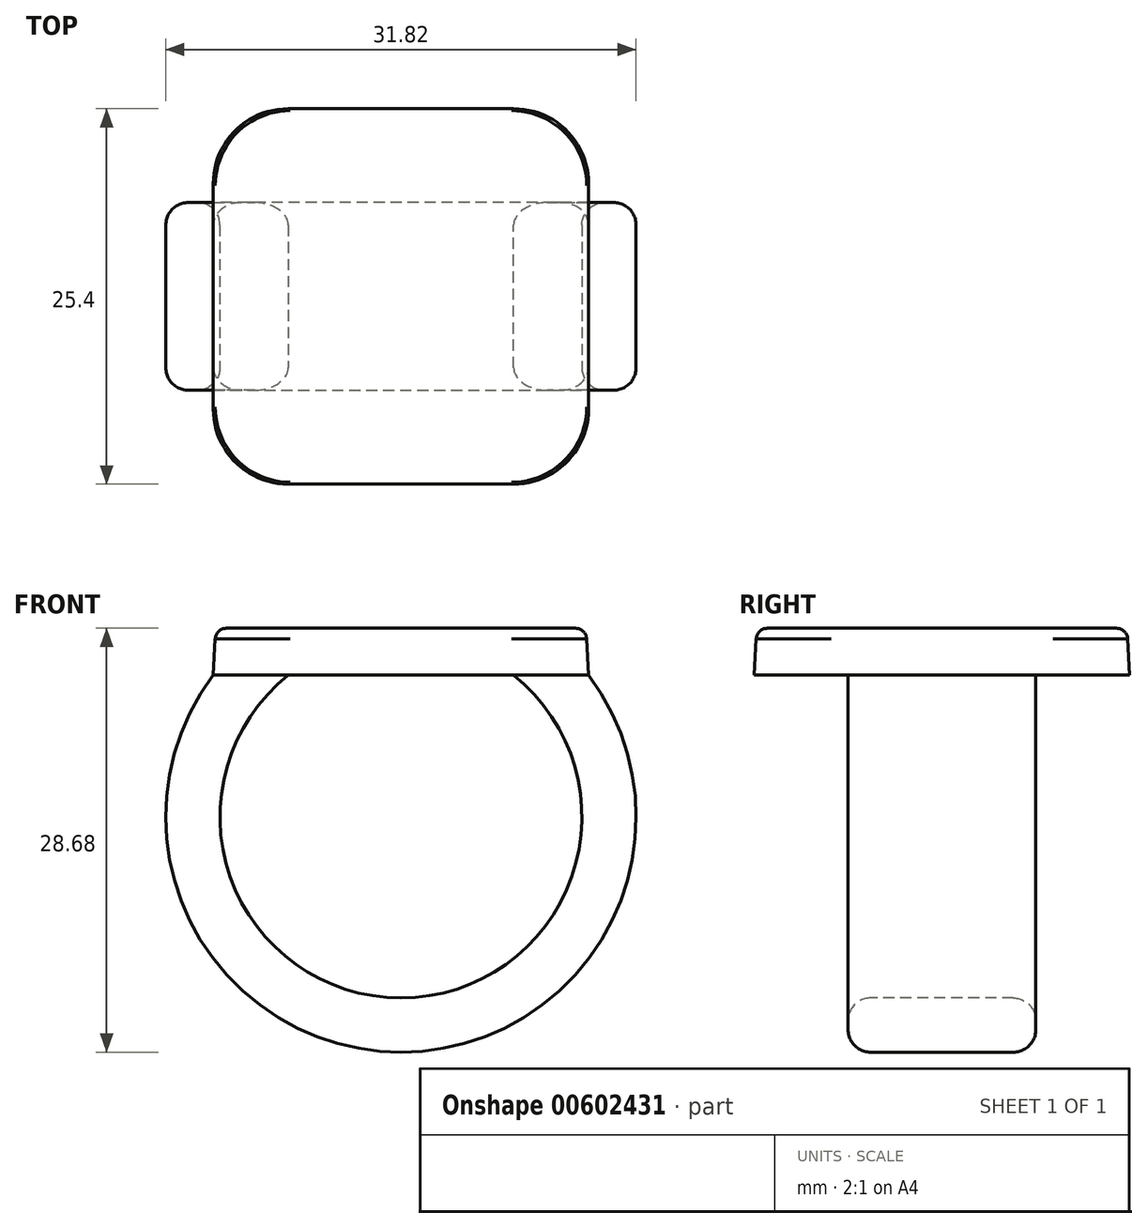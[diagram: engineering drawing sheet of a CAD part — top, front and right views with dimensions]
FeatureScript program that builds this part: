
annotation { "Feature Type Name" : "Feature", "Feature Type Description" : "" }
export const myFeature = defineFeature(function(context is Context, id is Id, definition is map)
    precondition{}
    {
        {
            var Q0;
            Q0=qCreatedBy(makeId("Top.planeOp"),FACE);
            var sketch = newSketch(context, id + "F0", { "sketchPlane" : qUnion([Q0])});
            skLineSegment(sketch, "E0.bottom", {"start": v(12.7, -12.7) * mm, "end": v(-12.7, -12.7) * mm});
            skLineSegment(sketch, "E0.top", {"start": v(12.7, 12.7) * mm, "end": v(-12.7, 12.7) * mm});
            skLineSegment(sketch, "E0.left", {"start": v(12.7, -12.7) * mm, "end": v(12.7, 12.7) * mm});
            skLineSegment(sketch, "E0.right", {"start": v(-12.7, -12.7) * mm, "end": v(-12.7, 12.7) * mm});
            skPoint(sketch, "E0.middle", {"position": v(0, 0) * mm});
            skSolve(sketch);
        }
        {
            var Q0;
            Q0=qSketchRegion(id+"F0",true);
            extrude(context, id + "F1", {"entities" : qUnion([Q0]), "depth" : 3.17 * mm, "offsetDistance" : 25.4 * mm, "hasDraft" : true, "draftAngle" : 3 * degree, "draftPullDirection" : true});
        }
        {
            var Q0;
            Q0=qCreatedBy(makeId("Front.planeOp"),FACE);
            var sketch = newSketch(context, id + "F2", { "sketchPlane" : qUnion([Q0])});
            skArc(sketch, "E1", {"start": v(-10.16, 0) * mm, "mid": v(0, -23.56) * mm, "end": v(10.16, 0) * mm});
            skSolve(sketch);
        }
        {
            var Q0;
            Q0=makeQuery(id+"F1.opExtrude","CAP_FACE",FACE,{"disambiguationData":[OSD([sQuery(id+"F0.wireOp",EDGE,"E0.bottom"),sQuery(id+"F0.wireOp",EDGE,"E0.top"),sQuery(id+"F0.wireOp",EDGE,"E0.left"),sQuery(id+"F0.wireOp",EDGE,"E0.right")])],"isStart":true});
            var sketch = newSketch(context, id + "F3", { "sketchPlane" : qUnion([Q0])});
            skLineSegment(sketch, "E2.bottom", {"start": v(-7.62, -6.35) * mm, "end": v(-12.7, -6.35) * mm});
            skLineSegment(sketch, "E2.top", {"start": v(-7.62, 6.35) * mm, "end": v(-12.7, 6.35) * mm});
            skLineSegment(sketch, "E2.left", {"start": v(-7.62, -6.35) * mm, "end": v(-7.62, 6.35) * mm});
            skLineSegment(sketch, "E2.right", {"start": v(-12.7, -6.35) * mm, "end": v(-12.7, 6.35) * mm});
            skPoint(sketch, "E2.middle", {"position": v(-10.16, 0) * mm});
            skSolve(sketch);
        }
        {
            var Q0;
            Q0=makeQuery(id+"F3.imprint","IMPRINT",FACE,{"disambiguationData":[TD([[makeQuery(id+"F3.imprint","IMPRINT",EDGE,{"derivedFrom":sQuery(id+"F3.wireOp",EDGE,"E2.bottom")}),-1.0]])]});
            var Q1;
            Q1=qConstructionFilter(qBodyType(qCreatedBy(id+"F2",EDGE),BodyType.WIRE),ConstructionObject.NO);
            sweep(context, id + "F4", {"operationType" : NewBodyOperationType.ADD, "profiles" : qUnion([Q0]), "path" : qUnion([Q1])});
        }
        {
            var Q0;
            Q0=qCreatedBy(makeId("Front.planeOp"),FACE);
            var sketch = newSketch(context, id + "F5", { "sketchPlane" : qUnion([Q0])});
            skLineSegment(sketch, "E3.0", {"start": v(10.16, 0) * mm, "end": v(7.62, 0) * mm});
            skLineSegment(sketch, "E3.1", {"start": v(10.01, -2.54) * mm, "end": v(10.16, 0) * mm});
            skArc(sketch, "E3.2", {"start": v(10.01, -2.54) * mm, "mid": v(8.9, -1.18) * mm, "end": v(7.62, 0) * mm});
            skPoint(sketch, "E4.trimOffspring.end.orphan", {"position": v(-12.7, 0) * mm});
            skPoint(sketch, "E5.orphan", {"position": v(-7.62, 0) * mm});
            skPoint(sketch, "E6.orphan", {"position": v(12.7, 0) * mm});
            skSolve(sketch);
        }
        {
            var Q0;
            Q0=qSketchRegion(id+"F5",true);
            var Q1;
            Q1=makeQuery(id+"F4.opSweep","SWEPT_FACE",FACE,{"disambiguationData":[OSD([sQuery(id+"F2.wireOp",EDGE,"E1"),sQuery(id+"F3.wireOp",EDGE,"E2.top")])]});
            var Q2;
            Q2=makeQuery(id+"F4.opSweep","SWEPT_FACE",FACE,{"disambiguationData":[OSD([sQuery(id+"F2.wireOp",EDGE,"E1"),sQuery(id+"F3.wireOp",EDGE,"E2.bottom")])]});
            extrude(context, id + "F6", {"entities" : qUnion([Q0]), "operationType" : NewBodyOperationType.ADD, "endBound" : BoundingType.UP_TO_SURFACE, "depth" : 25.4 * mm, "endBoundEntityFace" : qUnion([Q1]), "offsetDistance" : 25.4 * mm, "hasSecondDirection" : true, "secondDirectionBound" : SecondDirectionBoundingType.UP_TO_SURFACE, "secondDirectionOppositeDirection" : true, "secondDirectionDepth" : 25.4 * mm, "secondDirectionBoundEntityFace" : qUnion([Q2])});
        }
        {
            var Q0;
            Q0=makeQuery(id+"F1.opExtrude","SWEPT_EDGE",EDGE,{"disambiguationData":[OSD([sQuery(id+"F0.wireOp",EDGE,"E0.top"),sQuery(id+"F0.wireOp",EDGE,"E0.left")])]});
            var Q1;
            Q1=makeQuery(id+"F1.opExtrude","SWEPT_EDGE",EDGE,{"disambiguationData":[OSD([sQuery(id+"F0.wireOp",EDGE,"E0.bottom"),sQuery(id+"F0.wireOp",EDGE,"E0.left")])]});
            var Q2;
            Q2=makeQuery(id+"F1.opExtrude","SWEPT_EDGE",EDGE,{"disambiguationData":[OSD([sQuery(id+"F0.wireOp",EDGE,"E0.bottom"),sQuery(id+"F0.wireOp",EDGE,"E0.right")])]});
            var Q3;
            Q3=makeQuery(id+"F1.opExtrude","SWEPT_EDGE",EDGE,{"disambiguationData":[OSD([sQuery(id+"F0.wireOp",EDGE,"E0.top"),sQuery(id+"F0.wireOp",EDGE,"E0.right")])]});
            fillet(context, id + "F7", {"entities" : qUnion([Q0, Q1, Q2, Q3]), "radius" : 5.08 * mm, "tangentPropagation" : true, "allowEdgeOverflow" : false});
        }
        {
            var Q0;
            Q0=makeQuery(id+"F4.opSweep","SWEPT_EDGE",EDGE,{"disambiguationData":[OSD([sQuery(id+"F0.wireOp",EDGE,"E0.right"),sQuery(id+"F2.wireOp",EDGE,"E1"),sQuery(id+"F3.wireOp",EDGE,"E2.bottom"),sQuery(id+"F3.wireOp",EDGE,"E2.right")])]});
            var Q1;
            {var subQ0=sQuery(id+"F3.wireOp",EDGE,"E2.bottom");var subQ1=sQuery(id+"F2.wireOp",EDGE,"E1");Q1=makeQuery(id+"F6.boolean.opBoolean","MERGE",EDGE,{"derivedFrom":[makeQuery(id+"F4.opSweep","SWEPT_EDGE",EDGE,{"disambiguationData":[OSD([subQ1,subQ0,sQuery(id+"F3.wireOp",EDGE,"E2.left")])]}),makeQuery(id+"F6.opExtrude","TWEAK_EDGE",EDGE,{"derivedFrom":[makeQuery(id+"F4.opSweep","SWEPT_FACE",FACE,{"disambiguationData":[OSD([subQ1,subQ0])]}),makeQuery(id+"F5.imprint","IMPRINT",EDGE,{"derivedFrom":sQuery(id+"F5.wireOp",EDGE,"E3.2")})]})]});}
            var Q2;
            Q2=makeQuery(id+"F4.opSweep","SWEPT_EDGE",EDGE,{"disambiguationData":[OSD([sQuery(id+"F0.wireOp",EDGE,"E0.right"),sQuery(id+"F2.wireOp",EDGE,"E1"),sQuery(id+"F3.wireOp",EDGE,"E2.top"),sQuery(id+"F3.wireOp",EDGE,"E2.right")])]});
            var Q3;
            {var subQ0=sQuery(id+"F3.wireOp",EDGE,"E2.top");var subQ1=sQuery(id+"F2.wireOp",EDGE,"E1");Q3=makeQuery(id+"F6.boolean.opBoolean","MERGE",EDGE,{"derivedFrom":[makeQuery(id+"F4.opSweep","SWEPT_EDGE",EDGE,{"disambiguationData":[OSD([subQ1,subQ0,sQuery(id+"F3.wireOp",EDGE,"E2.left")])]}),makeQuery(id+"F6.opExtrude","TWEAK_EDGE",EDGE,{"derivedFrom":[makeQuery(id+"F4.opSweep","SWEPT_FACE",FACE,{"disambiguationData":[OSD([subQ1,subQ0])]}),makeQuery(id+"F5.imprint","IMPRINT",EDGE,{"derivedFrom":sQuery(id+"F5.wireOp",EDGE,"E3.2")})]})]});}
            fillet(context, id + "F8", {"entities" : qUnion([Q0, Q1, Q2, Q3]), "radius" : 1.52 * mm, "tangentPropagation" : true, "allowEdgeOverflow" : false});
        }
        {
            var Q0;
            Q0=makeQuery(id+"F1.opExtrude","CAP_FACE",FACE,{"disambiguationData":[OSD([sQuery(id+"F0.wireOp",EDGE,"E0.bottom"),sQuery(id+"F0.wireOp",EDGE,"E0.top"),sQuery(id+"F0.wireOp",EDGE,"E0.left"),sQuery(id+"F0.wireOp",EDGE,"E0.right")])],"isStart":false});
            fillet(context, id + "F9", {"entities" : qUnion([Q0]), "radius" : 0.76 * mm, "tangentPropagation" : true, "allowEdgeOverflow" : false});
        }
    });
